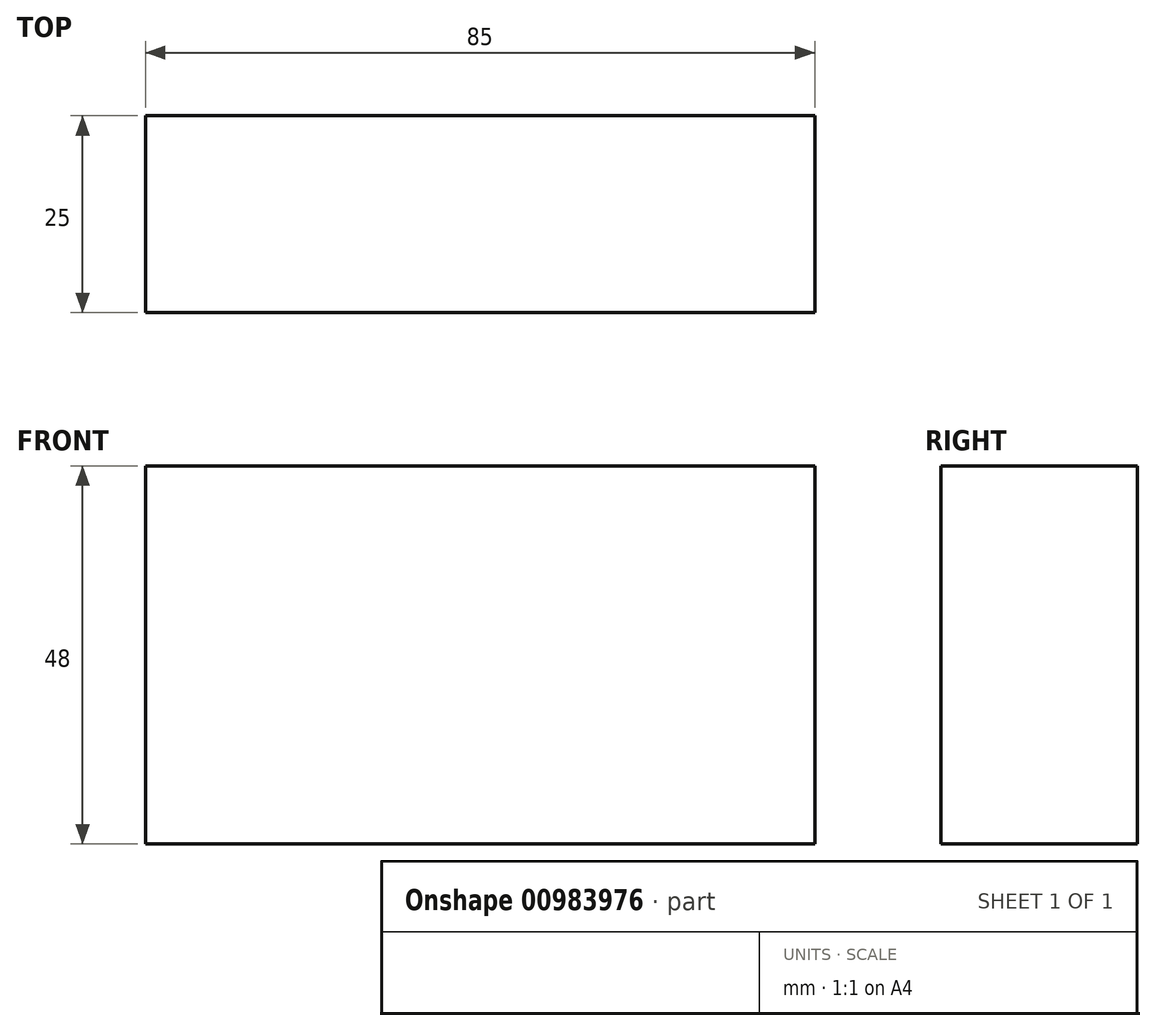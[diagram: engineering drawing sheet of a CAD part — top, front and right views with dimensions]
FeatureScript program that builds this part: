
annotation { "Feature Type Name" : "Feature", "Feature Type Description" : "" }
export const myFeature = defineFeature(function(context is Context, id is Id, definition is map)
    precondition{}
    {
        {
            var Q0;
            Q0=qCreatedBy(makeId("Front.planeOp"),FACE);
            var sketch = newSketch(context, id + "F0", { "sketchPlane" : qUnion([Q0])});
            skLineSegment(sketch, "E0.bottom", {"start": v(0, 0) * mm, "end": v(-19.27, 0) * mm});
            skLineSegment(sketch, "E0.top", {"start": v(0, 0) * mm, "end": v(-19.27, 0) * mm});
            skLineSegment(sketch, "E0.left", {"start": v(0, 0) * mm, "end": v(0, 0) * mm});
            skLineSegment(sketch, "E0.right", {"start": v(-19.27, 0) * mm, "end": v(-19.27, 0) * mm});
            skLineSegment(sketch, "E1.bottom", {"start": v(-19.27, 0) * mm, "end": v(65.73, 0) * mm});
            skLineSegment(sketch, "E1.top", {"start": v(-19.27, 48) * mm, "end": v(65.73, 48) * mm});
            skLineSegment(sketch, "E1.left", {"start": v(-19.27, 0) * mm, "end": v(-19.27, 48) * mm});
            skLineSegment(sketch, "E1.right", {"start": v(65.73, 0) * mm, "end": v(65.73, 48) * mm});
            skSolve(sketch);
        }
        {
            var Q0;
            Q0=makeQuery(id+"F0.imprint","IMPRINT",FACE,{"disambiguationData":[TD([[makeQuery(id+"F0.imprint","IMPRINT",EDGE,{"derivedFrom":sQuery(id+"F0.wireOp",EDGE,"E1.top")}),-1.0]])]});
            extrude(context, id + "F1", {"entities" : qUnion([Q0]), "endBound" : BoundingType.SYMMETRIC, "depth" : 25 * mm, "offsetDistance" : 25 * mm});
        }
    });
